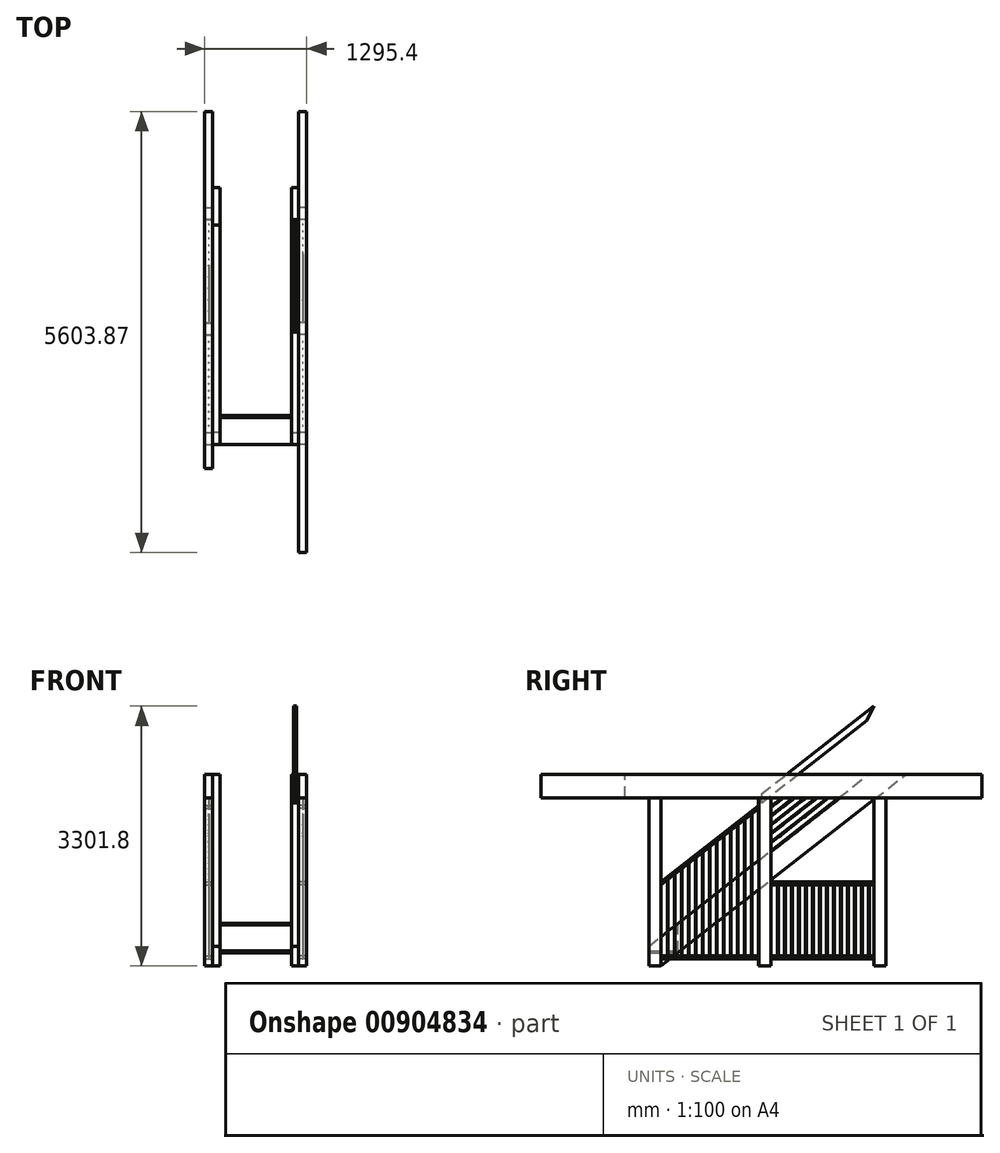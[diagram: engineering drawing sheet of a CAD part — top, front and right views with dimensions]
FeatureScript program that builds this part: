
annotation { "Feature Type Name" : "Feature", "Feature Type Description" : "" }
export const myFeature = defineFeature(function(context is Context, id is Id, definition is map)
    precondition{}
    {
        {
            var Q0;
            Q0=qCreatedBy(makeId("Front.planeOp"),FACE);
            var sketch = newSketch(context, id + "F0", { "sketchPlane" : qUnion([Q0])});
            skLineSegment(sketch, "E0", {"start": v(-546.1, 0) * mm, "end": v(546.1, 0) * mm});
            skSolve(sketch);
        }
        {
            var Q0;
            Q0=sQuery(id+"F0.wireOp",VERTEX,"E0.end");
            var Q1;
            Q1=qCreatedBy(makeId("Right.planeOp"),FACE);
            cPlane(context, id + "F1", {"entities" : qUnion([Q0, Q1]), "cplaneType" : CPlaneType.PLANE_POINT, "offset" : 25.4 * mm, "width" : 152.4 * mm, "height" : 152.4 * mm});
        }
        {
            var Q0;
            Q0=qCreatedBy(id+"F1.planeOp",FACE);
            var sketch = newSketch(context, id + "F2", { "sketchPlane" : qUnion([Q0])});
            skLineSegment(sketch, "E1.bottom", {"start": v(0, 0) * mm, "end": v(152.4, 0) * mm});
            skLineSegment(sketch, "E1.top", {"start": v(0, 2133.6) * mm, "end": v(152.4, 2133.6) * mm});
            skLineSegment(sketch, "E1.left", {"start": v(0, 0) * mm, "end": v(0, 2133.6) * mm});
            skLineSegment(sketch, "E1.right", {"start": v(152.4, 0) * mm, "end": v(152.4, 2133.6) * mm});
            skLineSegment(sketch, "E2.bottom", {"start": v(1397, 0) * mm, "end": v(1552.58, 0) * mm});
            skLineSegment(sketch, "E2.top", {"start": v(1397, 2133.6) * mm, "end": v(1552.57, 2133.6) * mm});
            skLineSegment(sketch, "E2.left", {"start": v(1397, 0) * mm, "end": v(1397, 2133.6) * mm});
            skLineSegment(sketch, "E2.right", {"start": v(1552.58, 0) * mm, "end": v(1552.57, 2133.6) * mm});
            skLineSegment(sketch, "E3.bottom", {"start": v(2860.68, 0) * mm, "end": v(3013.08, 0) * mm});
            skLineSegment(sketch, "E3.top", {"start": v(2860.68, 2133.6) * mm, "end": v(3013.07, 2133.6) * mm});
            skLineSegment(sketch, "E3.left", {"start": v(2860.68, 0) * mm, "end": v(2860.68, 2133.6) * mm});
            skLineSegment(sketch, "E3.right", {"start": v(3013.08, 0) * mm, "end": v(3013.07, 2133.6) * mm});
            skLineSegment(sketch, "E4.bottom", {"start": v(-1371.6, 2432.05) * mm, "end": v(4232.28, 2432.05) * mm});
            skLineSegment(sketch, "E4.top", {"start": v(-1371.6, 2133.6) * mm, "end": v(4232.28, 2133.6) * mm, "construction": true});
            skLineSegment(sketch, "E4.left", {"start": v(-1371.6, 2432.05) * mm, "end": v(-1371.6, 2133.6) * mm});
            skLineSegment(sketch, "E4.right", {"start": v(4232.28, 2432.05) * mm, "end": v(4232.28, 2133.6) * mm});
            skSolve(sketch);
        }
        {
            var Q0;
            Q0=qSketchRegion(id+"F2",true);
            extrude(context, id + "F3", {"entities" : qUnion([Q0]), "depth" : 101.6 * mm, "offsetDistance" : 25.4 * mm});
        }
        {
            var Q0;
            Q0=sQuery(id+"F0.wireOp",VERTEX,"E0.start");
            var Q1;
            Q1=qCreatedBy(makeId("Right.planeOp"),FACE);
            cPlane(context, id + "F4", {"entities" : qUnion([Q0, Q1]), "cplaneType" : CPlaneType.PLANE_POINT, "offset" : 25.4 * mm, "width" : 152.4 * mm, "height" : 152.4 * mm});
        }
        {
            var Q0;
            Q0=qCreatedBy(id+"F4.planeOp",FACE);
            var sketch = newSketch(context, id + "F5", { "sketchPlane" : qUnion([Q0])});
            skLineSegment(sketch, "E5.bottom", {"start": v(1390.65, 0) * mm, "end": v(1543.05, 0) * mm});
            skLineSegment(sketch, "E5.top", {"start": v(1390.65, 2133.6) * mm, "end": v(1543.05, 2133.6) * mm});
            skLineSegment(sketch, "E5.left", {"start": v(1390.65, 0) * mm, "end": v(1390.65, 2133.6) * mm});
            skLineSegment(sketch, "E5.right", {"start": v(1543.05, 0) * mm, "end": v(1543.05, 2133.6) * mm});
            skLineSegment(sketch, "E6.bottom", {"start": v(2863.85, 0) * mm, "end": v(3009.9, 0) * mm});
            skLineSegment(sketch, "E6.top", {"start": v(2863.85, 2133.6) * mm, "end": v(3009.9, 2133.6) * mm});
            skLineSegment(sketch, "E6.left", {"start": v(2863.85, 0) * mm, "end": v(2863.85, 2133.6) * mm});
            skLineSegment(sketch, "E6.right", {"start": v(3009.9, 0) * mm, "end": v(3009.9, 2133.6) * mm});
            skLineSegment(sketch, "E7.0.0", {"start": v(152.4, 2133.6) * mm, "end": v(0, 2133.6) * mm});
            skLineSegment(sketch, "E7.0.1", {"start": v(0, 2133.6) * mm, "end": v(0, 0) * mm});
            skLineSegment(sketch, "E7.0.2", {"start": v(0, 0) * mm, "end": v(152.4, 0) * mm});
            skLineSegment(sketch, "E7.0.3", {"start": v(152.4, 0) * mm, "end": v(152.4, 2133.6) * mm});
            skSolve(sketch);
        }
        {
            var Q0;
            Q0=qSketchRegion(id+"F5",true);
            extrude(context, id + "F6", {"entities" : qUnion([Q0]), "oppositeDirection" : true, "depth" : 101.6 * mm, "offsetDistance" : 25.4 * mm});
        }
        {
            var Q0;
            Q0=qCreatedBy(id+"F1.planeOp",FACE);
            var sketch = newSketch(context, id + "F7", { "sketchPlane" : qUnion([Q0])});
            skLineSegment(sketch, "E8.0", {"start": v(-1371.6, 2133.6) * mm, "end": v(4232.28, 2133.6) * mm});
            skLineSegment(sketch, "E9.0", {"start": v(-1371.6, 2432.05) * mm, "end": v(-1371.6, 2133.6) * mm});
            skLineSegment(sketch, "E10.0", {"start": v(-1371.6, 2432.05) * mm, "end": v(4232.28, 2432.05) * mm});
            skLineSegment(sketch, "E11.0", {"start": v(4232.28, 2432.05) * mm, "end": v(4232.28, 2133.6) * mm});
            skSolve(sketch);
        }
        {
            var Q0;
            Q0=makeQuery(id+"F7.imprint","IMPRINT",FACE,{"disambiguationData":[TD([[makeQuery(id+"F7.imprint","IMPRINT",EDGE,{"derivedFrom":sQuery(id+"F7.wireOp",EDGE,"E8.0")}),1.0]])]});
            var Q1;
            Q1=makeQuery(id+"F3.opExtrude","CAP_FACE",FACE,{"disambiguationData":[OSD([sQuery(id+"F2.wireOp",EDGE,"E1.bottom"),sQuery(id+"F2.wireOp",EDGE,"E1.top"),sQuery(id+"F2.wireOp",EDGE,"E1.left"),sQuery(id+"F2.wireOp",EDGE,"E1.right")])],"isStart":false});
            extrude(context, id + "F8", {"entities" : qUnion([Q0]), "endBound" : BoundingType.UP_TO_SURFACE, "depth" : 25.4 * mm, "endBoundEntityFace" : qUnion([Q1]), "offsetDistance" : 25.4 * mm});
        }
        {
            var Q0;
            Q0=qCreatedBy(id+"F4.planeOp",FACE);
            var sketch = newSketch(context, id + "F9", { "sketchPlane" : qUnion([Q0])});
            skLineSegment(sketch, "E12.0.0", {"start": v(4232.28, 2432.05) * mm, "end": v(4232.28, 2133.6) * mm});
            skLineSegment(sketch, "E12.0.1", {"start": v(4232.28, 2133.6) * mm, "end": v(-304.8, 2133.6) * mm});
            skLineSegment(sketch, "E12.0.3", {"start": v(-304.8, 2432.05) * mm, "end": v(4232.28, 2432.05) * mm});
            skLineSegment(sketch, "E13", {"start": v(-304.8, 2432.05) * mm, "end": v(-304.8, 2133.6) * mm});
            skPoint(sketch, "E12.0.2.end.orphan", {"position": v(-1371.6, 2432.05) * mm});
            skPoint(sketch, "E14.orphan", {"position": v(-1371.6, 2133.6) * mm});
            skSolve(sketch);
        }
        {
            var Q0;
            Q0=qSketchRegion(id+"F9",true);
            var Q1;
            Q1=makeQuery(id+"F6.opExtrude","CAP_FACE",FACE,{"disambiguationData":[OSD([sQuery(id+"F5.wireOp",EDGE,"E7.0.0"),sQuery(id+"F5.wireOp",EDGE,"E7.0.1"),sQuery(id+"F5.wireOp",EDGE,"E7.0.2"),sQuery(id+"F5.wireOp",EDGE,"E7.0.3")])],"isStart":false});
            extrude(context, id + "F10", {"entities" : qUnion([Q0]), "endBound" : BoundingType.UP_TO_SURFACE, "oppositeDirection" : true, "depth" : 25.4 * mm, "endBoundEntityFace" : qUnion([Q1]), "offsetDistance" : 25.4 * mm});
        }
        {
            var Q0;
            Q0=qCreatedBy(id+"F1.planeOp",FACE);
            var sketch = newSketch(context, id + "F11", { "sketchPlane" : qUnion([Q0])});
            skLineSegment(sketch, "E15.0", {"start": v(0, 0) * mm, "end": v(0, 251.61) * mm});
            skLineSegment(sketch, "E16", {"start": v(0, 251.61) * mm, "end": v(2790.83, 2432.05) * mm});
            skLineSegment(sketch, "E17", {"start": v(152.4, 0) * mm, "end": v(3265.28, 2432.05) * mm});
            skPoint(sketch, "E18.orphan", {"position": v(0, 2133.6) * mm});
            skPoint(sketch, "E19.orphan", {"position": v(152.4, 2133.6) * mm});
            skLineSegment(sketch, "E20.0", {"start": v(0, 0) * mm, "end": v(152.4, 0) * mm});
            skLineSegment(sketch, "E21.0", {"start": v(2790.83, 2432.05) * mm, "end": v(3265.28, 2432.05) * mm});
            skPoint(sketch, "E22.orphan", {"position": v(4232.28, 2432.05) * mm});
            skPoint(sketch, "E23.orphan", {"position": v(-1371.6, 2432.05) * mm});
            skPoint(sketch, "E24.0.end.orphan", {"position": v(3013.07, 2133.6) * mm});
            skPoint(sketch, "E24.0.start.orphan", {"position": v(3013.08, 0) * mm});
            skSolve(sketch);
        }
        {
            var Q0;
            Q0=qSketchRegion(id+"F11",true);
            extrude(context, id + "F12", {"entities" : qUnion([Q0]), "oppositeDirection" : true, "depth" : 92.07 * mm, "offsetDistance" : 25.4 * mm});
        }
        {
            var Q0;
            Q0=makeQuery(id+"F12.opExtrude","SWEPT_BODY",BODY,{"disambiguationData":[OSD([sQuery(id+"F11.wireOp",EDGE,"E15.0"),sQuery(id+"F11.wireOp",EDGE,"E16"),sQuery(id+"F11.wireOp",EDGE,"E17"),sQuery(id+"F11.wireOp",EDGE,"E20.0"),sQuery(id+"F11.wireOp",EDGE,"E21.0")])]});
            var Q1;
            Q1=qCreatedBy(makeId("Right.planeOp"),FACE);
            mirror(context, id + "F13", {"entities" : qUnion([Q0]), "mirrorPlane" : qUnion([Q1])});
        }
        {
            var Q0;
            Q0=makeQuery(id+"F3.opExtrude","CAP_FACE",FACE,{"disambiguationData":[OSD([sQuery(id+"F2.wireOp",EDGE,"E1.bottom"),sQuery(id+"F2.wireOp",EDGE,"E1.top"),sQuery(id+"F2.wireOp",EDGE,"E1.left"),sQuery(id+"F2.wireOp",EDGE,"E1.right")])],"isStart":false});
            var Q1;
            Q1=makeQuery(id+"F2.imprint","IMPRINT",FACE,{"disambiguationData":[TD([[makeQuery(id+"F2.imprint","IMPRINT",EDGE,{"derivedFrom":sQuery(id+"F2.wireOp",EDGE,"E1.bottom")}),1.0]])]});
            cPlane(context, id + "F14", {"entities" : qUnion([Q0, Q1]), "cplaneType" : CPlaneType.MID_PLANE, "offset" : 25.4 * mm, "width" : 152.4 * mm, "height" : 152.4 * mm});
        }
        {
            var Q0;
            Q0=qCreatedBy(id+"F14.planeOp",FACE);
            var sketch = newSketch(context, id + "F15", { "sketchPlane" : qUnion([Q0])});
            skLineSegment(sketch, "E25.0", {"start": v(152.4, 1028.7) * mm, "end": v(152.4, 1066.8) * mm, "construction": true});
            skLineSegment(sketch, "E26.0", {"start": v(1397, 1028.7) * mm, "end": v(1397, 1066.8) * mm, "construction": true});
            skLineSegment(sketch, "E27.bottom", {"start": v(152.4, 1066.8) * mm, "end": v(1397, 1066.8) * mm, "construction": true});
            skLineSegment(sketch, "E27.top", {"start": v(152.4, 1028.7) * mm, "end": v(1397, 1028.7) * mm, "construction": true});
            skPoint(sketch, "E28.orphan", {"position": v(152.4, 2133.6) * mm});
            skPoint(sketch, "E29.orphan", {"position": v(1397, 2133.6) * mm});
            skPoint(sketch, "E30.orphan", {"position": v(1397, 0) * mm});
            skPoint(sketch, "E31.orphan", {"position": v(152.4, 0) * mm});
            skLineSegment(sketch, "E32.bottom", {"start": v(1552.58, 1066.8) * mm, "end": v(2860.68, 1066.8) * mm});
            skLineSegment(sketch, "E32.top", {"start": v(1552.58, 1028.7) * mm, "end": v(2860.68, 1028.7) * mm});
            skLineSegment(sketch, "E32.left", {"start": v(1552.58, 1066.8) * mm, "end": v(1552.58, 1028.7) * mm});
            skLineSegment(sketch, "E32.right", {"start": v(2860.68, 1066.8) * mm, "end": v(2860.68, 1028.7) * mm});
            skLineSegment(sketch, "E33.bottom", {"start": v(152.4, 127) * mm, "end": v(1397, 127) * mm});
            skLineSegment(sketch, "E33.top", {"start": v(152.4, 88.9) * mm, "end": v(1397, 88.9) * mm});
            skLineSegment(sketch, "E33.left", {"start": v(152.4, 127) * mm, "end": v(152.4, 88.9) * mm});
            skLineSegment(sketch, "E33.right", {"start": v(1397, 127) * mm, "end": v(1397, 88.9) * mm});
            skLineSegment(sketch, "E34.bottom", {"start": v(1552.58, 127) * mm, "end": v(2860.68, 127) * mm});
            skLineSegment(sketch, "E34.top", {"start": v(1552.58, 88.9) * mm, "end": v(2860.68, 88.9) * mm});
            skLineSegment(sketch, "E34.left", {"start": v(1552.58, 127) * mm, "end": v(1552.58, 88.9) * mm});
            skLineSegment(sketch, "E34.right", {"start": v(2860.68, 127) * mm, "end": v(2860.68, 88.9) * mm});
            skLineSegment(sketch, "E35", {"start": v(152.4, 1066.8) * mm, "end": v(1397, 2039.19) * mm});
            skLineSegment(sketch, "E36", {"start": v(152.4, 1028.7) * mm, "end": v(1397, 2001.09) * mm});
            skLineSegment(sketch, "E37", {"start": v(1397, 2039.19) * mm, "end": v(1397, 2001.09) * mm});
            skLineSegment(sketch, "E38", {"start": v(152.4, 1028.7) * mm, "end": v(152.4, 1066.8) * mm});
            skSolve(sketch);
        }
        {
            var Q0;
            Q0=makeQuery(id+"F6.opExtrude","CAP_FACE",FACE,{"disambiguationData":[OSD([sQuery(id+"F5.wireOp",EDGE,"E7.0.0"),sQuery(id+"F5.wireOp",EDGE,"E7.0.1"),sQuery(id+"F5.wireOp",EDGE,"E7.0.2"),sQuery(id+"F5.wireOp",EDGE,"E7.0.3")])],"isStart":false});
            var Q1;
            Q1=makeQuery(id+"F6.opExtrude","CAP_FACE",FACE,{"disambiguationData":[OSD([sQuery(id+"F5.wireOp",EDGE,"E7.0.0"),sQuery(id+"F5.wireOp",EDGE,"E7.0.1"),sQuery(id+"F5.wireOp",EDGE,"E7.0.2"),sQuery(id+"F5.wireOp",EDGE,"E7.0.3")])],"isStart":true});
            cPlane(context, id + "F16", {"entities" : qUnion([Q0, Q1]), "cplaneType" : CPlaneType.MID_PLANE, "offset" : 25.4 * mm, "width" : 152.4 * mm, "height" : 152.4 * mm});
        }
        {
            var Q0;
            Q0=makeQuery(id+"F12.opExtrude","CAP_FACE",FACE,{"disambiguationData":[OSD([sQuery(id+"F11.wireOp",EDGE,"E15.0"),sQuery(id+"F11.wireOp",EDGE,"E16"),sQuery(id+"F11.wireOp",EDGE,"E17"),sQuery(id+"F11.wireOp",EDGE,"E20.0"),sQuery(id+"F11.wireOp",EDGE,"E21.0")])],"isStart":false});
            var Q1;
            Q1=makeQuery(id+"F12.opExtrude","CAP_FACE",FACE,{"disambiguationData":[OSD([sQuery(id+"F11.wireOp",EDGE,"E15.0"),sQuery(id+"F11.wireOp",EDGE,"E16"),sQuery(id+"F11.wireOp",EDGE,"E17"),sQuery(id+"F11.wireOp",EDGE,"E20.0"),sQuery(id+"F11.wireOp",EDGE,"E21.0")])],"isStart":true});
            cPlane(context, id + "F17", {"entities" : qUnion([Q0, Q1]), "cplaneType" : CPlaneType.MID_PLANE, "offset" : 25.4 * mm, "width" : 152.4 * mm, "height" : 152.4 * mm});
        }
        {
            var Q0;
            Q0=qCreatedBy(id+"F17.planeOp",FACE);
            var sketch = newSketch(context, id + "F18", { "sketchPlane" : qUnion([Q0])});
            skLineSegment(sketch, "E39.0", {"start": v(0, 364.43) * mm, "end": v(-1430.34, 1481.93) * mm, "construction": true});
            skLineSegment(sketch, "E40.0", {"start": v(0, 1066.8) * mm, "end": v(-1430.34, 2184.3) * mm, "construction": true});
            skLineSegment(sketch, "E41.0", {"start": v(0, 364.43) * mm, "end": v(0, 1066.8) * mm, "construction": true});
            skPoint(sketch, "E42.orphan", {"position": v(0, 2133.6) * mm});
            skPoint(sketch, "E43.orphan", {"position": v(0, 0) * mm});
            skLineSegment(sketch, "E44", {"start": v(-2860.68, 3301.8) * mm, "end": v(-2860.68, 2599.43) * mm});
            skLineSegment(sketch, "E45.0", {"start": v(-88.9, 1023.44) * mm, "end": v(-1430.34, 2071.49) * mm, "construction": true});
            skLineSegment(sketch, "E46.0", {"start": v(-88.9, 537.03) * mm, "end": v(-88.9, 1023.44) * mm, "construction": true});
            skLineSegment(sketch, "E47.trimOffspring", {"start": v(-2771.78, 3119.53) * mm, "end": v(-2771.78, 2633.12) * mm});
            skLineSegment(sketch, "E48.trimOffspring", {"start": v(-88.9, 537.03) * mm, "end": v(-1430.34, 1585.08) * mm, "construction": true});
            skLineSegment(sketch, "E49", {"start": v(-88.9, 1023.44) * mm, "end": v(0, 1066.8) * mm, "construction": true});
            skLineSegment(sketch, "E50", {"start": v(0, 364.43) * mm, "end": v(-88.9, 537.03) * mm, "construction": true});
            skLineSegment(sketch, "E51", {"start": v(-2771.78, 3119.53) * mm, "end": v(-2860.68, 3301.8) * mm});
            skLineSegment(sketch, "E52", {"start": v(-2771.78, 2633.12) * mm, "end": v(-2860.68, 2599.43) * mm});
            skPoint(sketch, "E53.0.start.orphan", {"position": v(-1552.58, 0) * mm});
            skPoint(sketch, "E54.0.start.orphan", {"position": v(-1397, 0) * mm});
            skLineSegment(sketch, "E55", {"start": v(-1397, 2045.44) * mm, "end": v(-1552.57, 2045.44) * mm, "construction": true});
            skLineSegment(sketch, "E56", {"start": v(-1474.79, 2045.44) * mm, "end": v(-1474.79, 1619.8) * mm, "construction": true});
            skLineSegment(sketch, "E57", {"start": v(-1430.34, 2184.3) * mm, "end": v(-1430.34, 1481.93) * mm});
            skLineSegment(sketch, "E58.MirrorCS", {"start": v(-1519.24, 2140.94) * mm, "end": v(-1519.24, 1654.53) * mm});
            skLineSegment(sketch, "E59", {"start": v(-1474.79, 1619.8) * mm, "end": v(-1238.8, 1921.85) * mm, "construction": true});
            skPoint(sketch, "E60.orphan", {"position": v(-1430.34, 2071.49) * mm});
            skPoint(sketch, "E61.orphan", {"position": v(-1430.34, 1585.08) * mm});
            skLineSegment(sketch, "E62", {"start": v(-1430.34, 2184.3) * mm, "end": v(-2860.68, 3301.8) * mm});
            skLineSegment(sketch, "E63", {"start": v(-1430.34, 2071.49) * mm, "end": v(-2771.78, 3119.53) * mm});
            skLineSegment(sketch, "E64", {"start": v(-1430.34, 1585.08) * mm, "end": v(-2771.78, 2633.12) * mm});
            skLineSegment(sketch, "E65", {"start": v(-1430.34, 1481.93) * mm, "end": v(-2860.68, 2599.43) * mm});
            skLineSegment(sketch, "E66", {"start": v(-1772.36, 1852.3) * mm, "end": v(-1552.58, 2133.6) * mm, "construction": true});
            skLineSegment(sketch, "E67.0", {"start": v(1371.6, 2133.6) * mm, "end": v(-4232.28, 2133.6) * mm, "construction": true});
            skLineSegment(sketch, "E68.0", {"start": v(-1552.58, 0) * mm, "end": v(-1552.57, 2133.6) * mm, "construction": true});
            skSolve(sketch);
        }
        {
            var Q0;
            {var subQ5=sQuery(id+"F18.wireOp",EDGE,"E51");Q0=makeQuery(id+"F18.imprint","IMPRINT",FACE,{"disambiguationData":[TD([[makeQuery(id+"F18.imprint","IMPRINT",EDGE,{"derivedFrom":subQ5}),-1.0]])]});}
            extrude(context, id + "F19", {"entities" : qUnion([Q0]), "endBound" : BoundingType.SYMMETRIC, "depth" : 38.1 * mm, "offsetDistance" : 25.4 * mm});
        }
        {
            var Q0;
            Q0=qCreatedBy(makeId("Right.planeOp"),FACE);
            var sketch = newSketch(context, id + "F20", { "sketchPlane" : qUnion([Q0])});
            skLineSegment(sketch, "E69", {"start": v(0, 170.54) * mm, "end": v(370.68, 170.54) * mm});
            skLineSegment(sketch, "E70", {"start": v(370.68, 170.54) * mm, "end": v(370.68, 541.22) * mm});
            skLineSegment(sketch, "E71.0", {"start": v(345.28, 195.94) * mm, "end": v(345.28, 521.37) * mm});
            skLineSegment(sketch, "E72.0", {"start": v(0, 195.94) * mm, "end": v(345.28, 195.94) * mm});
            skLineSegment(sketch, "E73.0", {"start": v(345.28, 521.37) * mm, "end": v(370.68, 541.22) * mm});
            skPoint(sketch, "E74.orphan", {"position": v(2790.83, 2432.05) * mm});
            skPoint(sketch, "E75.orphan", {"position": v(0, 251.61) * mm});
            skLineSegment(sketch, "E76.0", {"start": v(0, 170.54) * mm, "end": v(0, 195.94) * mm});
            skPoint(sketch, "E77.orphan", {"position": v(0, 2133.6) * mm});
            skPoint(sketch, "E78.orphan", {"position": v(0, 0) * mm});
            skSolve(sketch);
        }
        {
            var Q0;
            Q0=qSketchRegion(id+"F20",true);
            extrude(context, id + "F21", {"entities" : qUnion([Q0]), "endBound" : BoundingType.UP_TO_NEXT, "depth" : 25.4 * mm, "offsetDistance" : 25.4 * mm, "hasSecondDirection" : true, "secondDirectionBound" : SecondDirectionBoundingType.UP_TO_NEXT, "secondDirectionOppositeDirection" : true, "secondDirectionDepth" : 25.4 * mm});
        }
        {
            var Q0;
            Q0 = qSketchRegion(id + "F15", true);
            extrude(context, id + "F22", {"entities" : qUnion([Q0]), "endBound" : BoundingType.SYMMETRIC, "depth" : 88.9 * mm, "offsetDistance" : 25.4 * mm});
        }
        {
            var Q0;
            Q0=makeQuery(id+"F22.opExtrude","SWEPT_FACE",FACE,{"disambiguationData":[OSD([sQuery(id+"F15.wireOp",EDGE,"E33.top")])]});
            var sketch = newSketch(context, id + "F23", { "sketchPlane" : qUnion([Q0])});
            skLineSegment(sketch, "E79", {"start": v(596.9, -330.2) * mm, "end": v(596.9, -152.4) * mm, "construction": true});
            skLineSegment(sketch, "E80", {"start": v(596.9, -508) * mm, "end": v(596.9, -330.2) * mm, "construction": true});
            skLineSegment(sketch, "E81", {"start": v(596.9, -685.8) * mm, "end": v(596.9, -508) * mm, "construction": true});
            skLineSegment(sketch, "E82", {"start": v(596.9, -863.6) * mm, "end": v(596.9, -685.8) * mm, "construction": true});
            skLineSegment(sketch, "E83", {"start": v(596.9, -1041.4) * mm, "end": v(596.9, -863.6) * mm, "construction": true});
            skLineSegment(sketch, "E84", {"start": v(596.9, -1219.2) * mm, "end": v(596.9, -1041.4) * mm, "construction": true});
            skLineSegment(sketch, "E85.bottom", {"start": v(622.3, -304.8) * mm, "end": v(571.5, -304.8) * mm, "construction": true});
            skLineSegment(sketch, "E85.top", {"start": v(622.3, -355.6) * mm, "end": v(571.5, -355.6) * mm, "construction": true});
            skLineSegment(sketch, "E85.left", {"start": v(622.3, -304.8) * mm, "end": v(622.3, -355.6) * mm, "construction": true});
            skLineSegment(sketch, "E85.right", {"start": v(571.5, -304.8) * mm, "end": v(571.5, -355.6) * mm, "construction": true});
            skPoint(sketch, "E85.middle", {"position": v(596.9, -330.2) * mm});
            skCircle(sketch, "E86", {"center": v(596.9, -241.3) * mm, "radius": 4.76 * mm});
            skCircle(sketch, "E87.0.1.0", {"center": v(596.9, -330.2) * mm, "radius": 4.76 * mm});
            skCircle(sketch, "E87.0.2.0", {"center": v(596.9, -419.1) * mm, "radius": 4.76 * mm});
            skCircle(sketch, "E87.0.3.0", {"center": v(596.9, -508) * mm, "radius": 4.76 * mm});
            skCircle(sketch, "E87.0.4.0", {"center": v(596.9, -596.9) * mm, "radius": 4.76 * mm});
            skCircle(sketch, "E87.0.5.0", {"center": v(596.9, -685.8) * mm, "radius": 4.76 * mm});
            skCircle(sketch, "E87.0.6.0", {"center": v(596.9, -774.7) * mm, "radius": 4.76 * mm});
            skCircle(sketch, "E87.0.7.0", {"center": v(596.9, -863.6) * mm, "radius": 4.76 * mm});
            skCircle(sketch, "E87.0.8.0", {"center": v(596.9, -952.5) * mm, "radius": 4.76 * mm});
            skCircle(sketch, "E87.0.9.0", {"center": v(596.9, -1041.4) * mm, "radius": 4.76 * mm});
            skCircle(sketch, "E87.0.10.0", {"center": v(596.9, -1130.3) * mm, "radius": 4.76 * mm});
            skCircle(sketch, "E87.0.11.0", {"center": v(596.9, -1219.2) * mm, "radius": 4.76 * mm});
            skCircle(sketch, "E87.0.12.0", {"center": v(596.9, -1308.1) * mm, "radius": 4.76 * mm});
            skLineSegment(sketch, "E87.direction1", {"start": v(596.9, -241.3) * mm, "end": v(622.3, -241.3) * mm, "construction": true});
            skLineSegment(sketch, "E87.direction2", {"start": v(596.9, -241.3) * mm, "end": v(596.9, -330.2) * mm, "construction": true});
            skSolve(sketch);
        }
        {
            var Q0;
            Q0=makeQuery(id+"F22.opExtrude","SWEPT_FACE",FACE,{"disambiguationData":[OSD([sQuery(id+"F15.wireOp",EDGE,"E34.top")])]});
            var sketch = newSketch(context, id + "F24", { "sketchPlane" : qUnion([Q0])});
            skCircle(sketch, "E88", {"center": v(596.9, -1641.48) * mm, "radius": 4.76 * mm});
            skLineSegment(sketch, "E89", {"start": v(596.9, -1552.58) * mm, "end": v(596.9, -1730.38) * mm, "construction": true});
            skCircle(sketch, "E90.0.1.0", {"center": v(596.9, -1730.38) * mm, "radius": 4.76 * mm});
            skCircle(sketch, "E90.0.2.0", {"center": v(596.9, -1819.28) * mm, "radius": 4.76 * mm});
            skCircle(sketch, "E90.0.3.0", {"center": v(596.9, -1908.18) * mm, "radius": 4.76 * mm});
            skCircle(sketch, "E90.0.4.0", {"center": v(596.9, -1997.08) * mm, "radius": 4.76 * mm});
            skCircle(sketch, "E90.0.5.0", {"center": v(596.9, -2085.98) * mm, "radius": 4.76 * mm});
            skCircle(sketch, "E90.0.6.0", {"center": v(596.9, -2174.88) * mm, "radius": 4.76 * mm});
            skCircle(sketch, "E90.0.7.0", {"center": v(596.9, -2263.78) * mm, "radius": 4.76 * mm});
            skCircle(sketch, "E90.0.8.0", {"center": v(596.9, -2352.68) * mm, "radius": 4.76 * mm});
            skCircle(sketch, "E90.0.9.0", {"center": v(596.9, -2441.58) * mm, "radius": 4.76 * mm});
            skCircle(sketch, "E90.0.10.0", {"center": v(596.9, -2530.47) * mm, "radius": 4.76 * mm});
            skCircle(sketch, "E90.0.11.0", {"center": v(596.9, -2619.38) * mm, "radius": 4.76 * mm});
            skCircle(sketch, "E90.0.12.0", {"center": v(596.9, -2708.28) * mm, "radius": 4.76 * mm});
            skLineSegment(sketch, "E90.direction1", {"start": v(596.9, -1641.48) * mm, "end": v(622.3, -1641.48) * mm, "construction": true});
            skLineSegment(sketch, "E90.direction2", {"start": v(596.9, -1641.48) * mm, "end": v(596.9, -1730.38) * mm, "construction": true});
            skCircle(sketch, "E91.0.0.13", {"center": v(596.9, -2797.18) * mm, "radius": 4.76 * mm});
            skSolve(sketch);
        }
        {
            var Q0;
            Q0 = qSketchRegion(id + "F23", true);
            var Q1;
            Q1=makeQuery(id+"F22.opExtrude","SWEPT_FACE",FACE,{"disambiguationData":[OSD([sQuery(id+"F15.wireOp",EDGE,"E36")])]});
            extrude(context, id + "F25", {"entities" : qUnion([Q0]), "endBound" : BoundingType.UP_TO_SURFACE, "oppositeDirection" : true, "depth" : 25.4 * mm, "endBoundEntityFace" : qUnion([Q1]), "offsetDistance" : 25.4 * mm});
        }
        {
            var Q0;
            Q0 = qSketchRegion(id + "F24", true);
            var Q1;
            Q1=makeQuery(id+"F22.opExtrude","SWEPT_FACE",FACE,{"disambiguationData":[OSD([sQuery(id+"F15.wireOp",EDGE,"E32.top")])]});
            extrude(context, id + "F26", {"entities" : qUnion([Q0]), "endBound" : BoundingType.UP_TO_SURFACE, "oppositeDirection" : true, "depth" : 25.4 * mm, "endBoundEntityFace" : qUnion([Q1]), "offsetDistance" : 25.4 * mm});
        }
        {
            var Q0;
            Q0=sQuery(id+"F18.wireOp",EDGE,"E66");
            cPlane(context, id + "F27", {"entities" : qUnion([Q0]), "cplaneType" : CPlaneType.LINE_ANGLE, "offset" : 25.4 * mm, "angle" : 90 * degree, "width" : 152.4 * mm, "height" : 152.4 * mm});
        }
        {
            var Q0;
            Q0=qCreatedBy(id+"F27.planeOp",FACE);
            var sketch = newSketch(context, id + "F28", { "sketchPlane" : qUnion([Q0])});
            skLineSegment(sketch, "E92.0", {"start": v(-647.7, 725.44) * mm, "end": v(-546.1, 725.44) * mm, "construction": true});
            skLineSegment(sketch, "E93", {"start": v(-596.9, 725.44) * mm, "end": v(-596.9, 0) * mm, "construction": true});
            skCircle(sketch, "E94", {"center": v(-596.9, 636.54) * mm, "radius": 4.76 * mm});
            skCircle(sketch, "E95.0.1.0", {"center": v(-596.9, 547.64) * mm, "radius": 4.76 * mm});
            skCircle(sketch, "E95.0.2.0", {"center": v(-596.9, 458.74) * mm, "radius": 4.76 * mm});
            skCircle(sketch, "E95.0.3.0", {"center": v(-596.9, 369.84) * mm, "radius": 4.76 * mm});
            skLineSegment(sketch, "E95.direction1", {"start": v(-596.9, 636.54) * mm, "end": v(-571.5, 636.54) * mm, "construction": true});
            skLineSegment(sketch, "E95.direction2", {"start": v(-596.9, 636.54) * mm, "end": v(-596.9, 547.64) * mm, "construction": true});
            skCircle(sketch, "E96.0.0.4", {"center": v(-596.9, 280.94) * mm, "radius": 4.76 * mm});
            skCircle(sketch, "E96.0.0.5", {"center": v(-596.9, 192.04) * mm, "radius": 4.76 * mm});
            skSolve(sketch);
        }
        {
            var Q0;
            Q0 = qSketchRegion(id + "F28", true);
            extrude(context, id + "F29", {"entities" : qUnion([Q0]), "endBound" : BoundingType.UP_TO_NEXT, "depth" : 25.4 * mm, "offsetDistance" : 25.4 * mm, "hasSecondDirection" : true, "secondDirectionBound" : SecondDirectionBoundingType.UP_TO_NEXT, "secondDirectionOppositeDirection" : true, "secondDirectionDepth" : 25.4 * mm});
        }
        {
            var Q0;
            Q0=makeQuery(id+"F22.opExtrude","SWEPT_BODY",BODY,{"disambiguationData":[OSD([sQuery(id+"F15.wireOp",EDGE,"E32.bottom"),sQuery(id+"F15.wireOp",EDGE,"E32.top"),sQuery(id+"F15.wireOp",EDGE,"E32.left"),sQuery(id+"F15.wireOp",EDGE,"E32.right")])]});
            var Q1;
            Q1=makeQuery(id+"F22.opExtrude","SWEPT_BODY",BODY,{"disambiguationData":[OSD([sQuery(id+"F15.wireOp",EDGE,"E34.bottom"),sQuery(id+"F15.wireOp",EDGE,"E34.top"),sQuery(id+"F15.wireOp",EDGE,"E34.left"),sQuery(id+"F15.wireOp",EDGE,"E34.right")])]});
            var Q2;
            Q2=makeQuery(id+"F26.opExtrude","SWEPT_BODY",BODY,{"disambiguationData":[OSD([sQuery(id+"F24.wireOp",EDGE,"E88")])]});
            var Q3;
            Q3=makeQuery(id+"F26.opExtrude","SWEPT_BODY",BODY,{"disambiguationData":[OSD([sQuery(id+"F24.wireOp",EDGE,"E90.0.1.0")])]});
            var Q4;
            Q4=makeQuery(id+"F26.opExtrude","SWEPT_BODY",BODY,{"disambiguationData":[OSD([sQuery(id+"F24.wireOp",EDGE,"E90.0.2.0")])]});
            var Q5;
            Q5=makeQuery(id+"F26.opExtrude","SWEPT_BODY",BODY,{"disambiguationData":[OSD([sQuery(id+"F24.wireOp",EDGE,"E90.0.3.0")])]});
            var Q6;
            Q6=makeQuery(id+"F26.opExtrude","SWEPT_BODY",BODY,{"disambiguationData":[OSD([sQuery(id+"F24.wireOp",EDGE,"E90.0.4.0")])]});
            var Q7;
            Q7=makeQuery(id+"F26.opExtrude","SWEPT_BODY",BODY,{"disambiguationData":[OSD([sQuery(id+"F24.wireOp",EDGE,"E90.0.5.0")])]});
            var Q8;
            Q8=makeQuery(id+"F26.opExtrude","SWEPT_BODY",BODY,{"disambiguationData":[OSD([sQuery(id+"F24.wireOp",EDGE,"E90.0.6.0")])]});
            var Q9;
            Q9=makeQuery(id+"F26.opExtrude","SWEPT_BODY",BODY,{"disambiguationData":[OSD([sQuery(id+"F24.wireOp",EDGE,"E90.0.7.0")])]});
            var Q10;
            Q10=makeQuery(id+"F26.opExtrude","SWEPT_BODY",BODY,{"disambiguationData":[OSD([sQuery(id+"F24.wireOp",EDGE,"E90.0.8.0")])]});
            var Q11;
            Q11=makeQuery(id+"F26.opExtrude","SWEPT_BODY",BODY,{"disambiguationData":[OSD([sQuery(id+"F24.wireOp",EDGE,"E90.0.9.0")])]});
            var Q12;
            Q12=makeQuery(id+"F26.opExtrude","SWEPT_BODY",BODY,{"disambiguationData":[OSD([sQuery(id+"F24.wireOp",EDGE,"E90.0.10.0")])]});
            var Q13;
            Q13=makeQuery(id+"F26.opExtrude","SWEPT_BODY",BODY,{"disambiguationData":[OSD([sQuery(id+"F24.wireOp",EDGE,"E90.0.11.0")])]});
            var Q14;
            Q14=makeQuery(id+"F26.opExtrude","SWEPT_BODY",BODY,{"disambiguationData":[OSD([sQuery(id+"F24.wireOp",EDGE,"E90.0.12.0")])]});
            var Q15;
            Q15=makeQuery(id+"F26.opExtrude","SWEPT_BODY",BODY,{"disambiguationData":[OSD([sQuery(id+"F24.wireOp",EDGE,"E91.0.0.13")])]});
            var Q16;
            Q16=makeQuery(id+"F22.opExtrude","SWEPT_BODY",BODY,{"disambiguationData":[OSD([sQuery(id+"F15.wireOp",EDGE,"E33.bottom"),sQuery(id+"F15.wireOp",EDGE,"E33.top"),sQuery(id+"F15.wireOp",EDGE,"E33.left"),sQuery(id+"F15.wireOp",EDGE,"E33.right")])]});
            var Q17;
            Q17=makeQuery(id+"F22.opExtrude","SWEPT_BODY",BODY,{"disambiguationData":[OSD([sQuery(id+"F15.wireOp",EDGE,"E35"),sQuery(id+"F15.wireOp",EDGE,"E36"),sQuery(id+"F15.wireOp",EDGE,"E37"),sQuery(id+"F15.wireOp",EDGE,"E38")])]});
            var Q18;
            Q18=makeQuery(id+"F25.opExtrude","SWEPT_BODY",BODY,{"disambiguationData":[OSD([sQuery(id+"F23.wireOp",EDGE,"E86")])]});
            var Q19;
            Q19=makeQuery(id+"F25.opExtrude","SWEPT_BODY",BODY,{"disambiguationData":[OSD([sQuery(id+"F23.wireOp",EDGE,"E87.0.1.0")])]});
            var Q20;
            Q20=makeQuery(id+"F25.opExtrude","SWEPT_BODY",BODY,{"disambiguationData":[OSD([sQuery(id+"F23.wireOp",EDGE,"E87.0.2.0")])]});
            var Q21;
            Q21=makeQuery(id+"F25.opExtrude","SWEPT_BODY",BODY,{"disambiguationData":[OSD([sQuery(id+"F23.wireOp",EDGE,"E87.0.3.0")])]});
            var Q22;
            Q22=makeQuery(id+"F25.opExtrude","SWEPT_BODY",BODY,{"disambiguationData":[OSD([sQuery(id+"F23.wireOp",EDGE,"E87.0.4.0")])]});
            var Q23;
            Q23=makeQuery(id+"F25.opExtrude","SWEPT_BODY",BODY,{"disambiguationData":[OSD([sQuery(id+"F23.wireOp",EDGE,"E87.0.5.0")])]});
            var Q24;
            Q24=makeQuery(id+"F25.opExtrude","SWEPT_BODY",BODY,{"disambiguationData":[OSD([sQuery(id+"F23.wireOp",EDGE,"E87.0.6.0")])]});
            var Q25;
            Q25=makeQuery(id+"F25.opExtrude","SWEPT_BODY",BODY,{"disambiguationData":[OSD([sQuery(id+"F23.wireOp",EDGE,"E87.0.7.0")])]});
            var Q26;
            Q26=makeQuery(id+"F25.opExtrude","SWEPT_BODY",BODY,{"disambiguationData":[OSD([sQuery(id+"F23.wireOp",EDGE,"E87.0.8.0")])]});
            var Q27;
            Q27=makeQuery(id+"F25.opExtrude","SWEPT_BODY",BODY,{"disambiguationData":[OSD([sQuery(id+"F23.wireOp",EDGE,"E87.0.9.0")])]});
            var Q28;
            Q28=makeQuery(id+"F25.opExtrude","SWEPT_BODY",BODY,{"disambiguationData":[OSD([sQuery(id+"F23.wireOp",EDGE,"E87.0.10.0")])]});
            var Q29;
            Q29=makeQuery(id+"F25.opExtrude","SWEPT_BODY",BODY,{"disambiguationData":[OSD([sQuery(id+"F23.wireOp",EDGE,"E87.0.11.0")])]});
            var Q30;
            Q30=makeQuery(id+"F25.opExtrude","SWEPT_BODY",BODY,{"disambiguationData":[OSD([sQuery(id+"F23.wireOp",EDGE,"E87.0.12.0")])]});
            var Q31;
            Q31=makeQuery(id+"F29.opExtrude","SWEPT_BODY",BODY,{"disambiguationData":[OSD([sQuery(id+"F28.wireOp",EDGE,"E96.0.0.4")])]});
            var Q32;
            Q32=makeQuery(id+"F29.opExtrude","SWEPT_BODY",BODY,{"disambiguationData":[OSD([sQuery(id+"F28.wireOp",EDGE,"E95.0.3.0")])]});
            var Q33;
            Q33=makeQuery(id+"F29.opExtrude","SWEPT_BODY",BODY,{"disambiguationData":[OSD([sQuery(id+"F28.wireOp",EDGE,"E95.0.2.0")])]});
            var Q34;
            Q34=makeQuery(id+"F29.opExtrude","SWEPT_BODY",BODY,{"disambiguationData":[OSD([sQuery(id+"F28.wireOp",EDGE,"E95.0.1.0")])]});
            var Q35;
            Q35=makeQuery(id+"F29.opExtrude","SWEPT_BODY",BODY,{"disambiguationData":[OSD([sQuery(id+"F28.wireOp",EDGE,"E94")])]});
            var Q36;
            Q36=qCreatedBy(makeId("Right.planeOp"),FACE);
            mirror(context, id + "F30", {"entities" : qUnion([Q0, Q1, Q2, Q3, Q4, Q5, Q6, Q7, Q8, Q9, Q10, Q11, Q12, Q13, Q14, Q15, Q16, Q17, Q18, Q19, Q20, Q21, Q22, Q23, Q24, Q25, Q26, Q27, Q28, Q29, Q30, Q31, Q32, Q33, Q34, Q35]), "mirrorPlane" : qUnion([Q36])});
        }
    });
